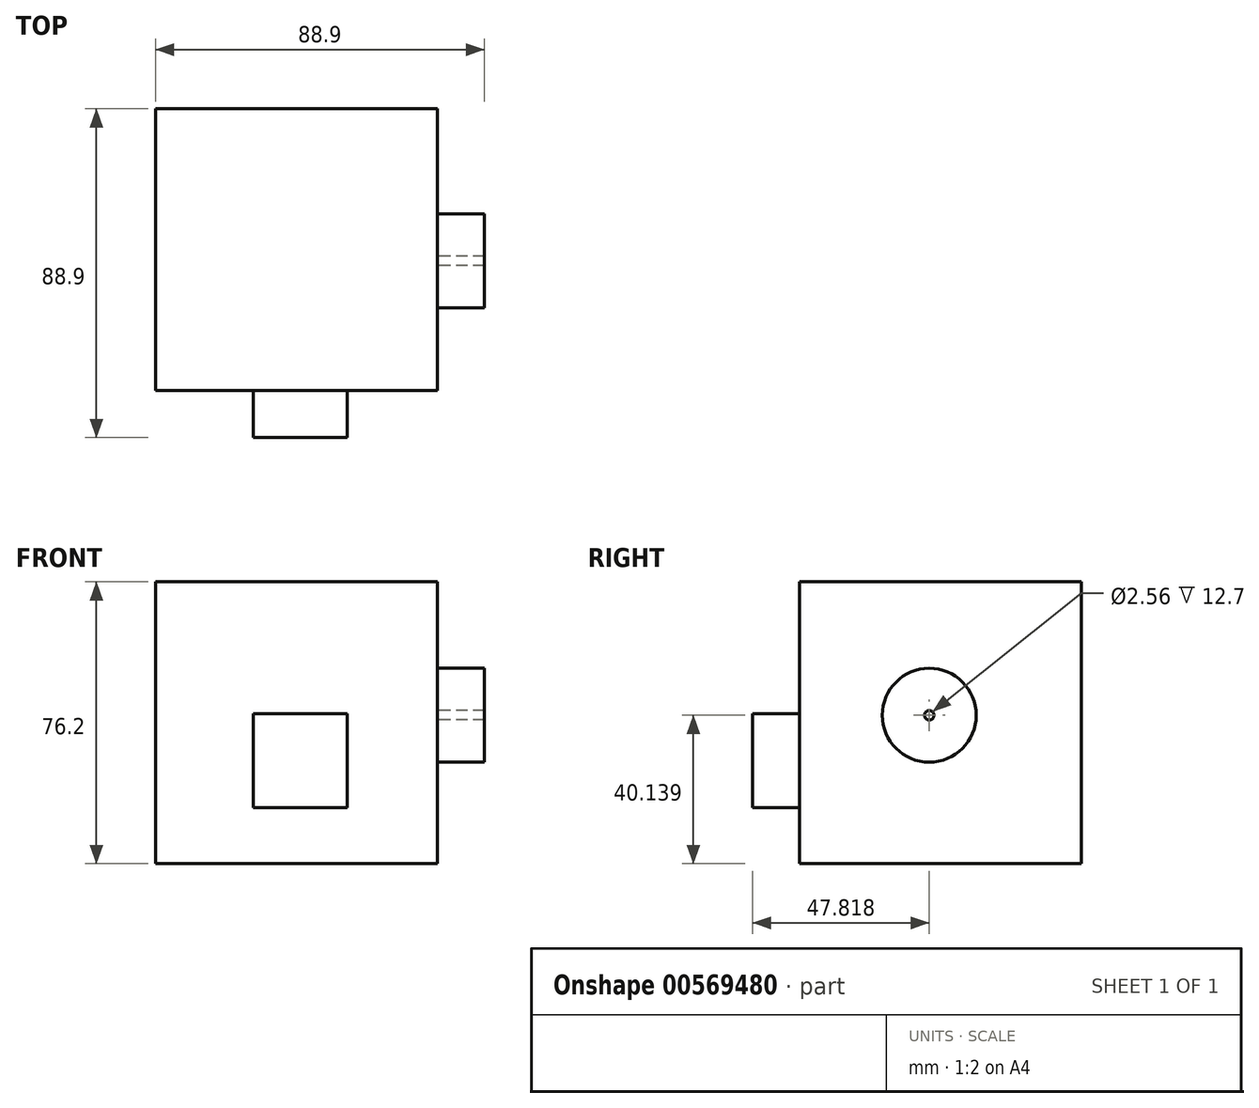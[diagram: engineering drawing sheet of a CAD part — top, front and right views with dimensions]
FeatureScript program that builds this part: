
annotation { "Feature Type Name" : "Feature", "Feature Type Description" : "" }
export const myFeature = defineFeature(function(context is Context, id is Id, definition is map)
    precondition{}
    {
        {
            var Q0;
            Q0=qCreatedBy(makeId("Front.planeOp"),FACE);
            var sketch = newSketch(context, id + "F0", { "sketchPlane" : qUnion([Q0])});
            skLineSegment(sketch, "E0.bottom", {"start": v(-38.98, 107.69) * mm, "end": v(37.22, 107.69) * mm});
            skLineSegment(sketch, "E0.top", {"start": v(-38.98, 31.49) * mm, "end": v(37.22, 31.49) * mm});
            skLineSegment(sketch, "E0.left", {"start": v(-38.98, 107.69) * mm, "end": v(-38.98, 31.49) * mm});
            skLineSegment(sketch, "E0.right", {"start": v(37.22, 107.69) * mm, "end": v(37.22, 31.49) * mm});
            skSolve(sketch);
        }
        {
            var Q0;
            Q0=makeQuery(id+"F0.imprint","IMPRINT",FACE,{"disambiguationData":[TD([[makeQuery(id+"F0.imprint","IMPRINT",EDGE,{"derivedFrom":sQuery(id+"F0.wireOp",EDGE,"E0.bottom")}),-1.0]])]});
            extrude(context, id + "F1", {"entities" : qUnion([Q0]), "depth" : 76.2 * mm, "offsetDistance" : 25.4 * mm});
        }
        {
            var Q0;
            Q0=makeQuery(id+"F1.opExtrude","CAP_FACE",FACE,{"disambiguationData":[OSD([sQuery(id+"F0.wireOp",EDGE,"E0.bottom"),sQuery(id+"F0.wireOp",EDGE,"E0.top"),sQuery(id+"F0.wireOp",EDGE,"E0.left"),sQuery(id+"F0.wireOp",EDGE,"E0.right")])],"isStart":false});
            var sketch = newSketch(context, id + "F2", { "sketchPlane" : qUnion([Q0])});
            skLineSegment(sketch, "E1.bottom", {"start": v(-12.59, 72) * mm, "end": v(12.81, 72) * mm});
            skLineSegment(sketch, "E1.top", {"start": v(-12.59, 46.6) * mm, "end": v(12.81, 46.6) * mm});
            skLineSegment(sketch, "E1.left", {"start": v(-12.59, 72) * mm, "end": v(-12.59, 46.6) * mm});
            skLineSegment(sketch, "E1.right", {"start": v(12.81, 72) * mm, "end": v(12.81, 46.6) * mm});
            skPoint(sketch, "E2.oppositeSnap0", {"position": v(0.11, 72) * mm});
            skLineSegment(sketch, "E2.bottom", {"start": v(0.11, 72) * mm, "end": v(0.11, 72) * mm});
            skLineSegment(sketch, "E2.top", {"start": v(0.11, 74.07) * mm, "end": v(0.11, 74.07) * mm});
            skLineSegment(sketch, "E2.left", {"start": v(0.11, 74.07) * mm, "end": v(0.11, 72) * mm});
            skLineSegment(sketch, "E2.right", {"start": v(0.11, 74.07) * mm, "end": v(0.11, 72) * mm});
            skSolve(sketch);
        }
        {
            var Q0;
            Q0=makeQuery(id+"F2.imprint","IMPRINT",FACE,{"disambiguationData":[TD([[makeQuery(id+"F2.imprint","IMPRINT",EDGE,{"derivedFrom":sQuery(id+"F2.wireOp",EDGE,"E1.top")}),1.0]])]});
            extrude(context, id + "F3", {"entities" : qUnion([Q0]), "operationType" : NewBodyOperationType.ADD, "depth" : 12.7 * mm, "offsetDistance" : 25.4 * mm});
        }
        {
            var Q0;
            Q0=makeQuery(id+"F1.opExtrude","SWEPT_FACE",FACE,{"disambiguationData":[OSD([sQuery(id+"F0.wireOp",EDGE,"E0.right")])]});
            var sketch = newSketch(context, id + "F4", { "sketchPlane" : qUnion([Q0])});
            skCircle(sketch, "E3", {"center": v(-41.08, 71.63) * mm, "radius": 12.7 * mm});
            skCircle(sketch, "E4", {"center": v(-41.08, 71.63) * mm, "radius": 1.28 * mm});
            skSolve(sketch);
        }
        {
            var Q0;
            Q0=makeQuery(id+"F4.imprint","IMPRINT",FACE,{"disambiguationData":[TD([[makeQuery(id+"F4.imprint","IMPRINT",EDGE,{"derivedFrom":sQuery(id+"F4.wireOp",EDGE,"E3")}),1.0]])]});
            extrude(context, id + "F5", {"entities" : qUnion([Q0]), "operationType" : NewBodyOperationType.ADD, "depth" : 12.7 * mm, "offsetDistance" : 25.4 * mm});
        }
    });
